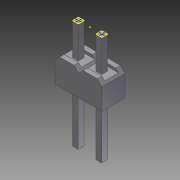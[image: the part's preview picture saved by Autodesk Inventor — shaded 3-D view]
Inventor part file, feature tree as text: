
AUTODESK INVENTOR PART (.ipt)
format: ipt  version: 2014 (Build 180170000, 170)  size: 97,792 bytes
history: native  units: mm (DEFAULTED — no unit token found)
features: other x2, sketch x1, projected_geometry x1
ambient origin geometry x8: Origin, YZ Plane, XZ Plane, XY Plane, X Axis, Y Axis, Z Axis, Center Point
bodies: Volumenkörper1 (feature_tree)
feature tree (4):
  sketch  "Skizze1"
  other  "Arbeitspunkt1"
  other  "Arbeitspunkt2"
  projected_geometry  "Projizierte Kontur1"
